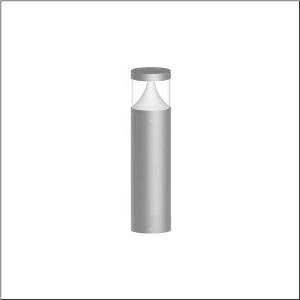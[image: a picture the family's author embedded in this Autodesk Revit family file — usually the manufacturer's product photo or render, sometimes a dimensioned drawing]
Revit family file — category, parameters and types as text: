
# Revit family: cl_31_poller_60_5cl434603
name_source: partatom
category: Lighting Fixtures
units: mm (PartAtom-declared; Revit-internal decimal feet)

## family parameters
Cut with Voids When Loaded = No
Host = Face
Light Source = No
Part Type = Normal
Room Calculation Point = No
Round Connector Dimension = Use Diameter
Shared = No

## types (1)
- --- (1 x LED, 1500 lm, 14 W, 3000K)
    Apparent Load = 14 VA
    CIE Flux Codes = 19 66 88 92 100
    Color Rendering = 80
    Color Temperature = 3000K
    Default Elevation = 1800 mm
    Description = CL 31 Bollard 60, bollard luminaire, primary light control with lens, of PC, primary optical cover: cover panel, of PC, transparent, secondary light control with reflector, of PC, primary light characteristic: asymmetric, LED, rated luminous flux: 1.500lm, luminous efficacy: 107lm/W, light colour: 830, colour temperature: 3000K, control gear: ECG DALI, with terminal, 5-pole, max. 2.5mm², mains connection: 220..240V, AC, 50/60Hz, rated input power: 14W, luminaire housing, of aluminium, powder-coated, Siteco® metallic grey, diameter: 170mm, height: 600mm, protection rating (complete): IP65, insulation class (complete): insulation class I (protective earthing), certification: CE, ENEC, impact resistance: IK10, permissible operating ambient temperature for outdoor applications: -20..+50°C, packaging unit: 1 piece
    Height = 200 mm  [stored 0.656168 ft]
    Lamp = 1 x LED
    Lamp Light Flux = 1500 lm
    Lamp Power = 14 W
    Lamp count = 1
    Length = 170 mm  [stored 0.557743 ft]
    Luminous efficacy = 107 lm/W
    Manufacturer = Siteco
    ModVariant = No
    Model = 5CL434603
    Mounting Place = Floor
    Mounting Type = Freestanding
    Number of Poles = 1
    OnlyDefault = Yes
    Power Factor = 1
    Product Name = CL 31 Poller 60
    Product group = bollard luminaire | freestanding
    ProductGroupID = 1303
    Protection Class = Protection class I
    Protection Degree = IP 65
    RLX_Detail_Level = 1
    RlxData = <blob elided: 63409 chars, md5=d565d304>
    Socket = socket
    Standby Power = 0 W
    System Light Flux = 1500 lm
    System Power = 14 W
    Type Comments = factory setting: luminous flux: 100 % | dim-lin: 254 | 350 mA
    Type Image = l_1006903.jpg
    URL = http://relux.com
    VarID = @adj_117007
    Voltage = 0 V
    Weight = 0.00 kg
    Width = 0 mm  [stored 0 ft]

note: [stored X ft] marks values corroborated as IEEE doubles in the binary element streams (Revit-internal decimal feet)

## geometry (parser evidence)
native form markers: Blend x4, Sweep x10
no freeform markers — native parametric forms only
